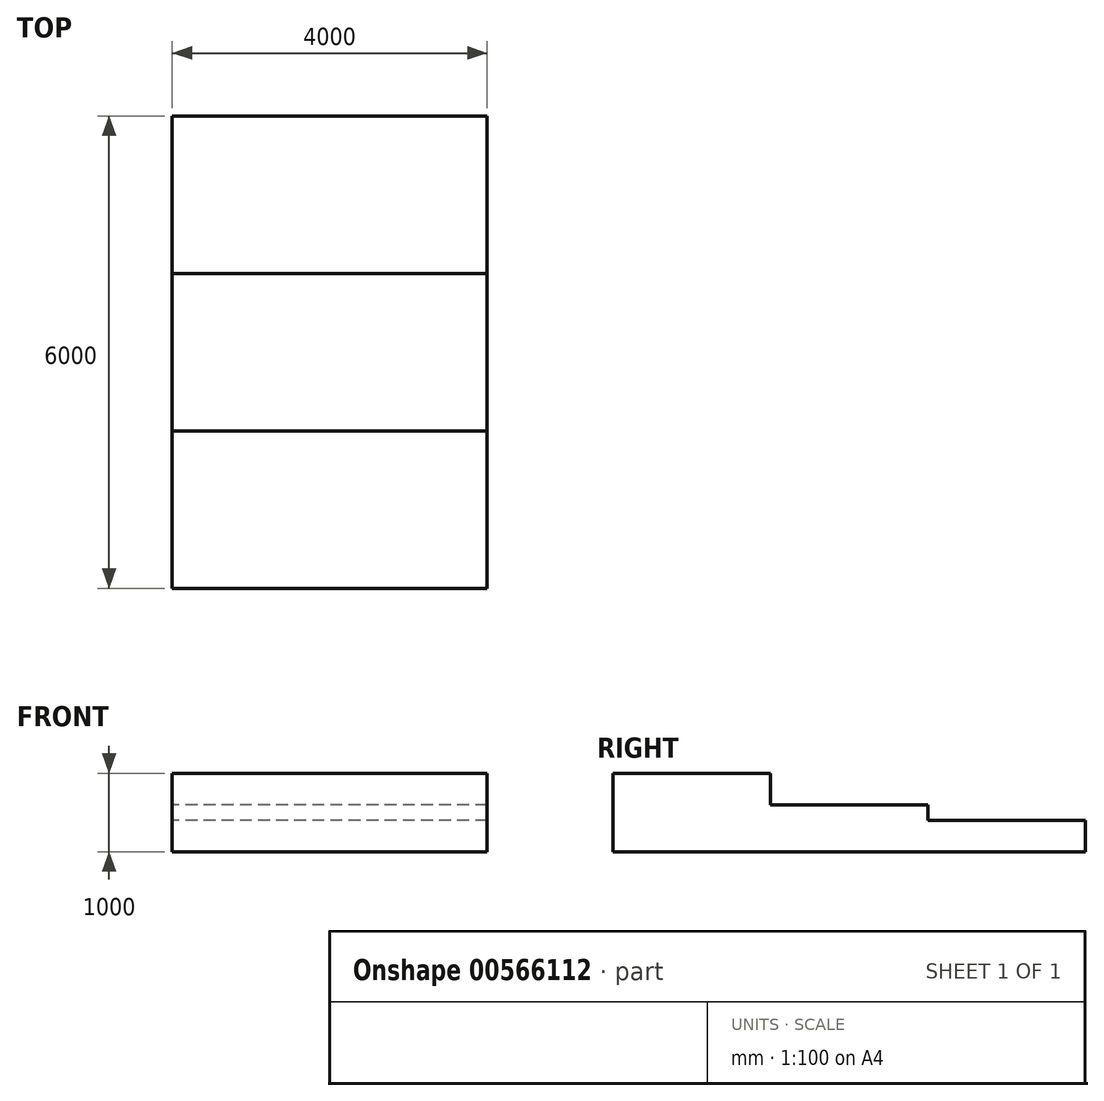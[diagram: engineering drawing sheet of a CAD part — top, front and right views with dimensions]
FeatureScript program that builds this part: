
annotation { "Feature Type Name" : "Feature", "Feature Type Description" : "" }
export const myFeature = defineFeature(function(context is Context, id is Id, definition is map)
    precondition{}
    {
        {
            var Q0;
            Q0=qCreatedBy(makeId("Right.planeOp"),FACE);
            var sketch = newSketch(context, id + "F0", { "sketchPlane" : qUnion([Q0])});
            skLineSegment(sketch, "E0", {"start": v(-4764.9, -1432.15) * mm, "end": v(1235.1, -1432.15) * mm});
            skLineSegment(sketch, "E1", {"start": v(1235.1, -1432.15) * mm, "end": v(1235.1, -1032.15) * mm});
            skLineSegment(sketch, "E2", {"start": v(1235.1, -1032.15) * mm, "end": v(-764.9, -1032.15) * mm});
            skLineSegment(sketch, "E3", {"start": v(-764.9, -1032.15) * mm, "end": v(-764.9, -832.15) * mm});
            skLineSegment(sketch, "E4", {"start": v(-764.9, -832.15) * mm, "end": v(-2764.9, -832.15) * mm});
            skLineSegment(sketch, "E5", {"start": v(-2764.9, -832.15) * mm, "end": v(-2764.9, -632.15) * mm});
            skLineSegment(sketch, "E6", {"start": v(-2764.9, -632.15) * mm, "end": v(-4764.9, -632.15) * mm});
            skLineSegment(sketch, "E7", {"start": v(-4764.9, -632.15) * mm, "end": v(-4764.9, -1432.15) * mm});
            skSolve(sketch);
        }
        {
            var Q0;
            Q0=makeQuery(id+"F0.imprint","IMPRINT",FACE,{"disambiguationData":[TD([[makeQuery(id+"F0.imprint","IMPRINT",EDGE,{"derivedFrom":sQuery(id+"F0.wireOp",EDGE,"E0")}),1.0]])]});
            extrude(context, id + "F1", {"entities" : qUnion([Q0]), "depth" : 4000 * mm, "offsetDistance" : 25 * mm});
        }
        {
            var Q0;
            Q0=makeQuery(id+"F1.opExtrude","SWEPT_FACE",FACE,{"disambiguationData":[OSD([sQuery(id+"F0.wireOp",EDGE,"E6")])]});
            extrude(context, id + "F2", {"entities" : qUnion([Q0]), "operationType" : NewBodyOperationType.ADD, "depth" : 200 * mm, "offsetDistance" : 25 * mm});
        }
    });
